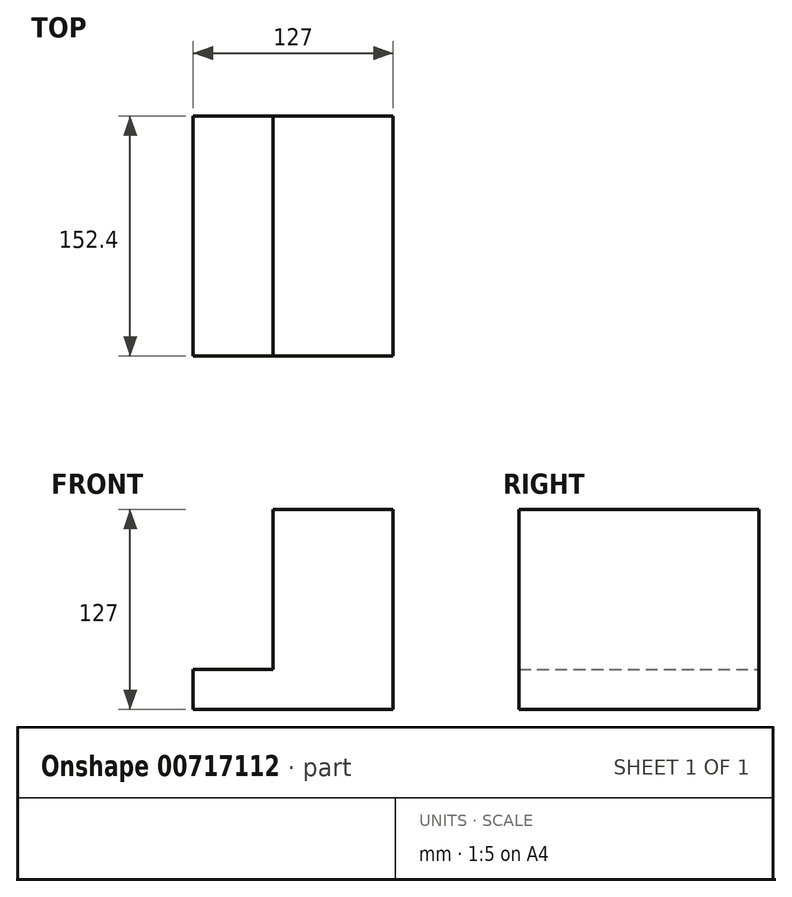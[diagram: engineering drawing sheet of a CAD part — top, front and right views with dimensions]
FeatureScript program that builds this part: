
annotation { "Feature Type Name" : "Feature", "Feature Type Description" : "" }
export const myFeature = defineFeature(function(context is Context, id is Id, definition is map)
    precondition{}
    {
        {
            var Q0;
            Q0=qCreatedBy(makeId("Front.planeOp"),FACE);
            var sketch = newSketch(context, id + "F0", { "sketchPlane" : qUnion([Q0])});
            skLineSegment(sketch, "E0", {"start": v(-61.47, -57.67) * mm, "end": v(65.53, -57.67) * mm});
            skLineSegment(sketch, "E1", {"start": v(65.53, -57.67) * mm, "end": v(65.53, 69.33) * mm});
            skLineSegment(sketch, "E2", {"start": v(65.53, 69.33) * mm, "end": v(-10.67, 69.33) * mm});
            skLineSegment(sketch, "E3", {"start": v(-10.67, 69.33) * mm, "end": v(-10.67, -32.27) * mm});
            skLineSegment(sketch, "E4", {"start": v(-10.67, -32.27) * mm, "end": v(-61.47, -32.27) * mm});
            skLineSegment(sketch, "E5", {"start": v(-61.47, -32.27) * mm, "end": v(-61.47, -57.67) * mm});
            skSolve(sketch);
        }
        {
            var Q0;
            Q0=makeQuery(id+"F0.imprint","IMPRINT",FACE,{"disambiguationData":[TD([[makeQuery(id+"F0.imprint","IMPRINT",EDGE,{"derivedFrom":sQuery(id+"F0.wireOp",EDGE,"E0")}),1.0]])]});
            extrude(context, id + "F1", {"entities" : qUnion([Q0]), "depth" : 152.4 * mm, "offsetDistance" : 25.4 * mm});
        }
    });
